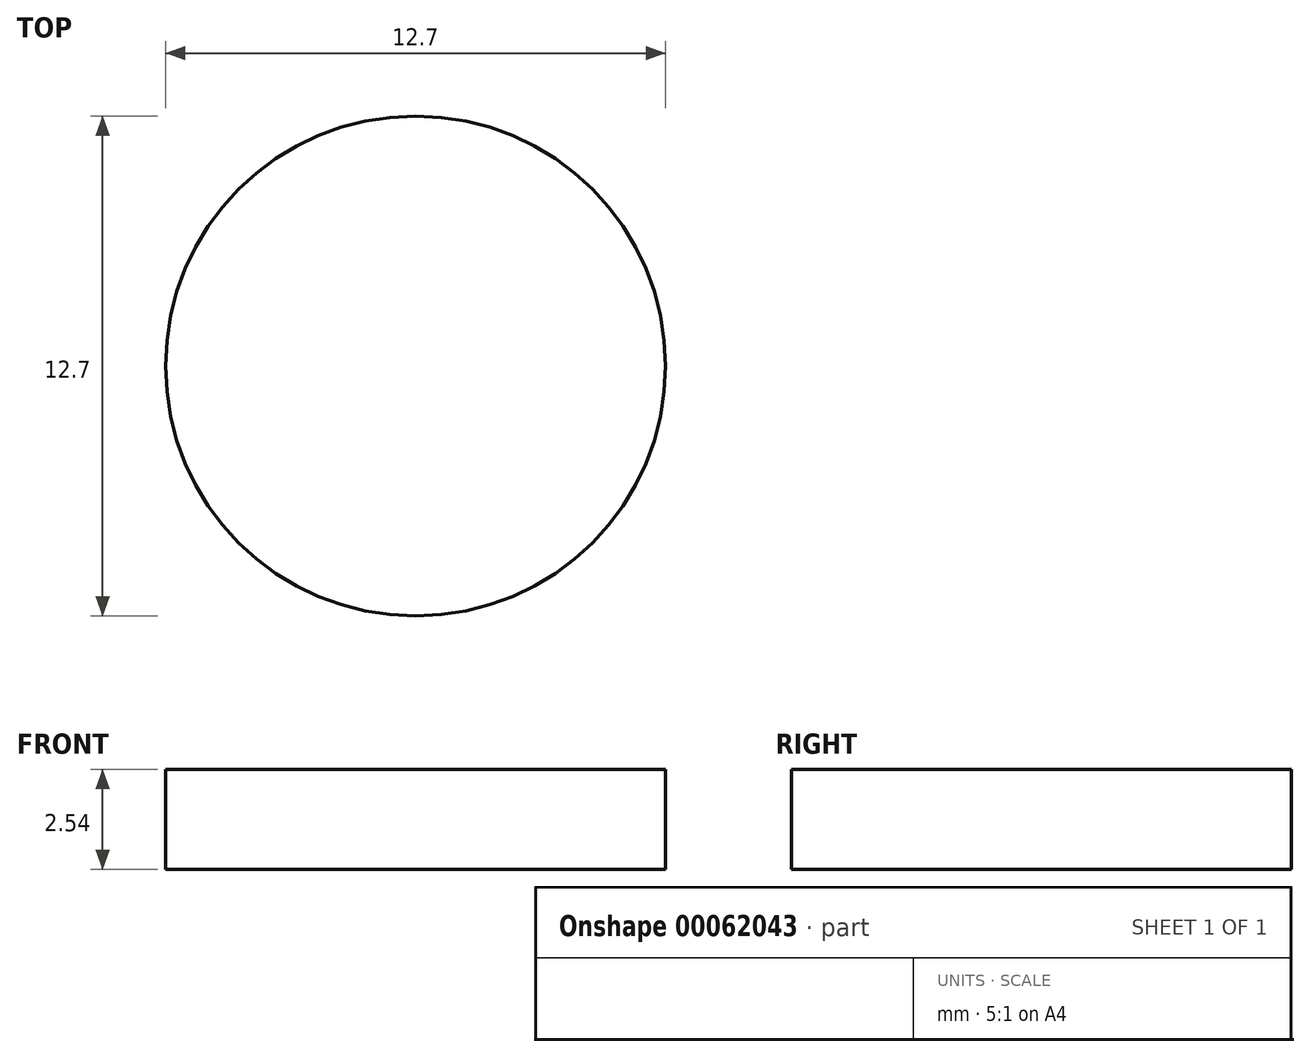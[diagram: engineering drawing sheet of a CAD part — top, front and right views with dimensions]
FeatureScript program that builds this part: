
annotation { "Feature Type Name" : "Feature", "Feature Type Description" : "" }
export const myFeature = defineFeature(function(context is Context, id is Id, definition is map)
    precondition{}
    {
        {
            var Q0;
            Q0=qCreatedBy(makeId("Top.planeOp"),FACE);
            var sketch = newSketch(context, id + "F0", { "sketchPlane" : qUnion([Q0])});
            skCircle(sketch, "E0", {"center": v(0, 0) * mm, "radius": 6.35 * mm});
            skSolve(sketch);
        }
        {
            var Q0;
            Q0 = qSketchRegion(id + "F0", true);
            extrude(context, id + "F1", {"entities" : qUnion([Q0]), "depth" : 2.54 * mm});
        }
    });
